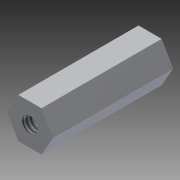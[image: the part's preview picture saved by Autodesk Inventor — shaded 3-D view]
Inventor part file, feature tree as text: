
AUTODESK INVENTOR PART (.ipt)
format: ipt  version: 2013 SP2 (Build 170200200, 200)  size: 78,848 bytes
history: native  units: in
note: dims shown in document units (in); Inventor stores cm internally (conversion verified against a paired STEP export)
features: sketch x2, extrude x1, hole x1
ambient origin geometry x8: Origin, YZ Plane, XZ Plane, XY Plane, X Axis, Y Axis, Z Axis, Center Point
bodies: Solid1 (feature_tree)
feature tree (4):
  extrude  "Extrusion1"  Depth=1.5in TaperAngle=0.0deg
  hole  "Hole1"  [1 undecoded]
  sketch  "Sketch1"  dims[d0=0.5in d1=1.5in d2=0.0in]
  sketch  "Sketch2"  dims[d3=0.196in d4=0.75in d5=0.375in d6=0.25in d7=0.5635in d8=1.0in d9=0.8108in]
note: 1 required parameter value undecoded (feature->parameter linkage not recoverable at this tier; creation-order binding heuristic only, values carry confidence <= 0.55)
